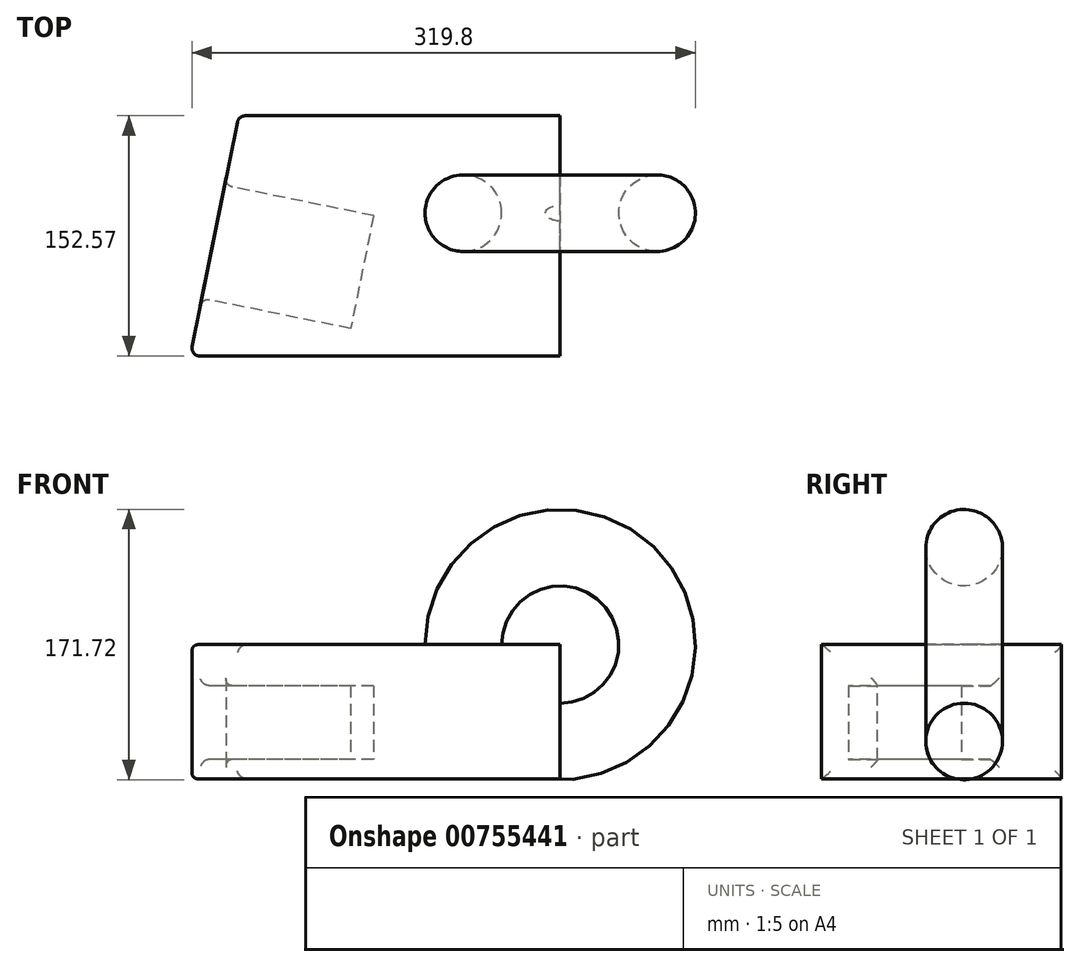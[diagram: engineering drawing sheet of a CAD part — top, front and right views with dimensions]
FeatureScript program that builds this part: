
annotation { "Feature Type Name" : "Feature", "Feature Type Description" : "" }
export const myFeature = defineFeature(function(context is Context, id is Id, definition is map)
    precondition{}
    {
        {
            var Q0;
            Q0=qCreatedBy(makeId("Top.planeOp"),FACE);
            var sketch = newSketch(context, id + "F0", { "sketchPlane" : qUnion([Q0])});
            skLineSegment(sketch, "E0", {"start": v(-235.07, -152.57) * mm, "end": v(0, -152.57) * mm});
            skLineSegment(sketch, "E1", {"start": v(-235.07, -152.57) * mm, "end": v(-204.14, 0) * mm});
            skLineSegment(sketch, "E2", {"start": v(-204.14, 0) * mm, "end": v(0, 0) * mm});
            skLineSegment(sketch, "E3", {"start": v(0, -152.57) * mm, "end": v(0, 0) * mm});
            skSolve(sketch);
        }
        {
            var Q0;
            Q0=makeQuery(id+"F0.imprint","IMPRINT",FACE,{"disambiguationData":[TD([[makeQuery(id+"F0.imprint","IMPRINT",EDGE,{"derivedFrom":sQuery(id+"F0.wireOp",EDGE,"E0")}),1.0]])]});
            extrude(context, id + "F1", {"entities" : qUnion([Q0]), "oppositeDirection" : true, "depth" : 85.34 * mm, "offsetDistance" : 25.4 * mm});
        }
        {
            var Q0;
            Q0=makeQuery(id+"F1.opExtrude","SWEPT_FACE",FACE,{"disambiguationData":[OSD([sQuery(id+"F0.wireOp",EDGE,"E1")])]});
            var sketch = newSketch(context, id + "F2", { "sketchPlane" : qUnion([Q0])});
            skLineSegment(sketch, "E4.bottom", {"start": v(85.78, -26.12) * mm, "end": v(158.97, -26.12) * mm});
            skLineSegment(sketch, "E4.top", {"start": v(85.78, -72.94) * mm, "end": v(158.97, -72.94) * mm});
            skLineSegment(sketch, "E4.left", {"start": v(85.78, -26.12) * mm, "end": v(85.78, -72.94) * mm});
            skLineSegment(sketch, "E4.right", {"start": v(158.97, -26.12) * mm, "end": v(158.97, -72.94) * mm});
            skSolve(sketch);
        }
        {
            var Q0;
            Q0=makeQuery(id+"F2.imprint","IMPRINT",FACE,{"disambiguationData":[TD([[makeQuery(id+"F2.imprint","IMPRINT",EDGE,{"derivedFrom":sQuery(id+"F2.wireOp",EDGE,"E4.bottom")}),-1.0]])]});
            extrude(context, id + "F3", {"entities" : qUnion([Q0]), "operationType" : NewBodyOperationType.REMOVE, "oppositeDirection" : true, "depth" : 96.52 * mm, "offsetDistance" : 25.4 * mm});
        }
        {
            var Q0;
            Q0=makeQuery(id+"F1.opExtrude","SWEPT_FACE",FACE,{"disambiguationData":[OSD([sQuery(id+"F0.wireOp",EDGE,"E1")])]});
            fillet(context, id + "F4", {"entities" : qUnion([Q0]), "radius" : 5.08 * mm, "tangentPropagation" : true, "allowEdgeOverflow" : false});
        }
        {
            var Q0;
            Q0=qCreatedBy(makeId("Right.planeOp"),FACE);
            var sketch = newSketch(context, id + "F5", { "sketchPlane" : qUnion([Q0])});
            skCircle(sketch, "E5", {"center": v(-61.87, 61.54) * mm, "radius": 24.33 * mm});
            skSolve(sketch);
        }
        {
            var Q0;
            Q0=makeQuery(id+"F5.imprint","IMPRINT",FACE,{"disambiguationData":[TD([[makeQuery(id+"F5.imprint","IMPRINT",EDGE,{"derivedFrom":sQuery(id+"F5.wireOp",EDGE,"E5")}),1.0]])]});
            var Q1;
            Q1=makeQuery(id+"F1.opExtrude","CAP_EDGE",EDGE,{"disambiguationData":[OSD([sQuery(id+"F0.wireOp",EDGE,"E3")])],"isStart":true});
            revolve(context, id + "F6", {"operationType" : NewBodyOperationType.ADD, "surfaceOperationType" : NewSurfaceOperationType.NEW, "entities" : qUnion([Q0]), "axis" : qUnion([Q1]), "revolveType" : RevolveType.FULL});
        }
    });
